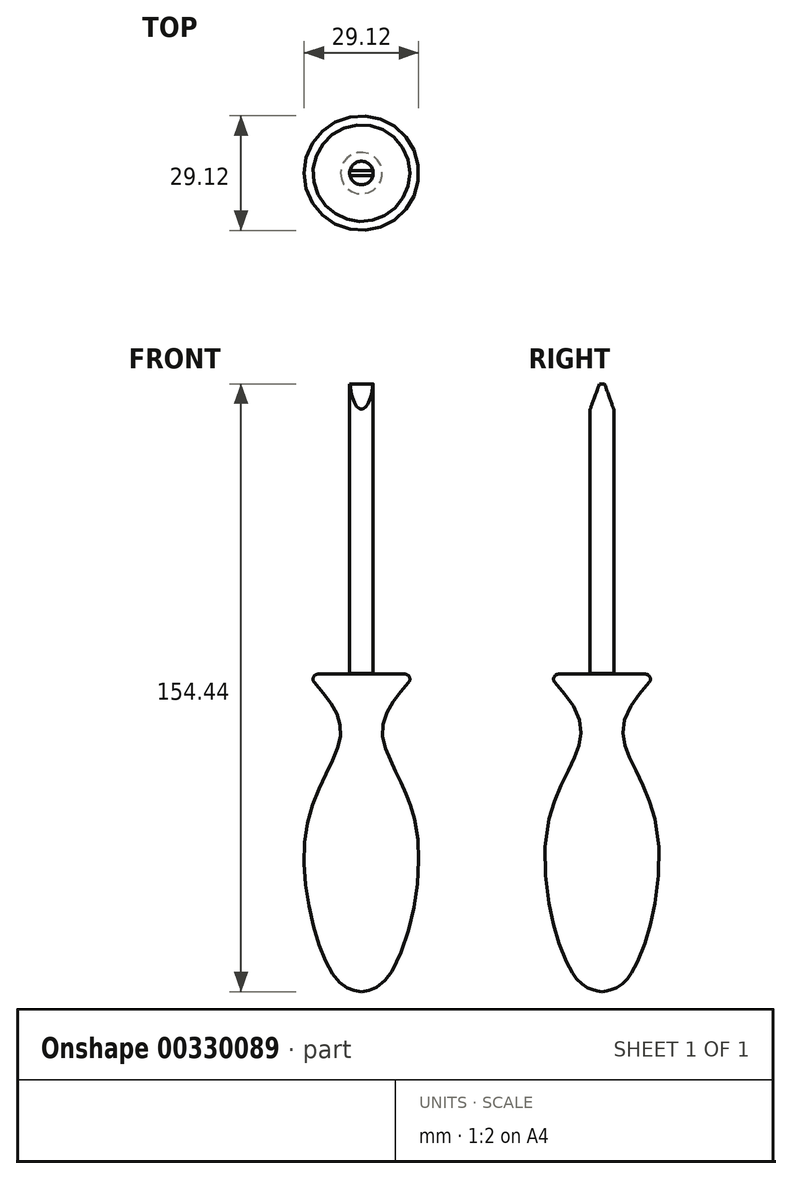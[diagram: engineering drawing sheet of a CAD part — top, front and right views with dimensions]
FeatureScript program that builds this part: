
annotation { "Feature Type Name" : "Feature", "Feature Type Description" : "" }
export const myFeature = defineFeature(function(context is Context, id is Id, definition is map)
    precondition{}
    {
        {
            var Q0;
            Q0=qCreatedBy(makeId("Front.planeOp"),FACE);
            var sketch = newSketch(context, id + "F0", { "sketchPlane" : qUnion([Q0])});
            skLineSegment(sketch, "E0", {"start": v(0, 12.38) * mm, "end": v(-13.91, 12.38) * mm});
            skFitSpline(sketch, "E1", {"points": [v(-13.91, 12.38) * mm, v(-5.27, -2.2) * mm, v(-13.91, -26.48) * mm, v(-6.62, -64.8) * mm, v(0, -68.31) * mm], "startDerivative": vector(57.37, -62.22) * mm, "endDerivative": vector(44.3, -7.4) * mm});
            skLineSegment(sketch, "E2", {"start": v(0, 12.38) * mm, "end": v(0, -68.31) * mm});
            skSolve(sketch);
        }
        {
            var Q0;
            Q0=makeQuery(id+"F0.imprint","IMPRINT",FACE,{"disambiguationData":[TD([[makeQuery(id+"F0.imprint","IMPRINT",EDGE,{"derivedFrom":sQuery(id+"F0.wireOp",EDGE,"E0")}),1.0]])]});
            var Q1;
            Q1=sQuery(id+"F0.wireOp",EDGE,"E2");
            revolve(context, id + "F1", {"entities" : qUnion([Q0]), "axis" : qUnion([Q1]), "revolveType" : RevolveType.FULL});
        }
        {
            var Q0;
            Q0=makeQuery(id+"F1.opRevolve","SWEPT_EDGE",EDGE,{"disambiguationData":[OSD([sQuery(id+"F0.wireOp",EDGE,"E0"),sQuery(id+"F0.wireOp",EDGE,"E1")])]});
            fillet(context, id + "F2", {"entities" : qUnion([Q0]), "radius" : 1.27 * mm, "tangentPropagation" : true, "allowEdgeOverflow" : false});
        }
        {
            var Q0;
            Q0=qCreatedBy(makeId("Front.planeOp"),FACE);
            var sketch = newSketch(context, id + "F3", { "sketchPlane" : qUnion([Q0])});
            skLineSegment(sketch, "E3", {"start": v(0, 12.56) * mm, "end": v(0, 86.13) * mm});
            skLineSegment(sketch, "E4", {"start": v(0, 86.13) * mm, "end": v(-3, 86.13) * mm});
            skLineSegment(sketch, "E5", {"start": v(-3, 86.13) * mm, "end": v(-3, 12.56) * mm});
            skLineSegment(sketch, "E6", {"start": v(-3, 12.56) * mm, "end": v(0, 12.56) * mm});
            skSolve(sketch);
        }
        {
            var Q0;
            Q0=makeQuery(id+"F3.imprint","IMPRINT",FACE,{"disambiguationData":[TD([[makeQuery(id+"F3.imprint","IMPRINT",EDGE,{"derivedFrom":sQuery(id+"F3.wireOp",EDGE,"E3")}),1.0]])]});
            var Q1;
            Q1=sQuery(id+"F3.wireOp",EDGE,"E3");
            revolve(context, id + "F4", {"entities" : qUnion([Q0]), "axis" : qUnion([Q1]), "revolveType" : RevolveType.FULL});
        }
        {
            var Q0;
            Q0=qCreatedBy(makeId("Top.planeOp"),FACE);
            cPlane(context, id + "F5", {"entities" : qUnion([Q0]), "cplaneType" : CPlaneType.OFFSET, "offset" : 96.52 * mm, "width" : 152.4 * mm, "height" : 152.4 * mm});
        }
        {
            var Q0;
            Q0=qCreatedBy(makeId("Top.planeOp"),FACE);
            cPlane(context, id + "F6", {"entities" : qUnion([Q0]), "cplaneType" : CPlaneType.OFFSET, "offset" : 86.06 * mm, "width" : 152.4 * mm, "height" : 152.4 * mm});
        }
        {
            var Q0;
            Q0=qCreatedBy(id+"F6.planeOp",FACE);
            var sketch = newSketch(context, id + "F7", { "sketchPlane" : qUnion([Q0])});
            skLineSegment(sketch, "E7", {"start": v(76.67, 0) * mm, "end": v(-76.37, 0) * mm, "construction": true});
            skSolve(sketch);
        }
        {
            var Q0;
            Q0=qCreatedBy(id+"F6.planeOp",FACE);
            var Q1;
            Q1=sQuery(id+"F7.wireOp",EDGE,"E7");
            cPlane(context, id + "F8", {"entities" : qUnion([Q0, Q1]), "cplaneType" : CPlaneType.LINE_ANGLE, "offset" : 25.4 * mm, "angle" : 20 * degree, "width" : 152.4 * mm, "height" : 152.4 * mm});
        }
        {
            var Q0;
            Q0=qCreatedBy(id+"F8.planeOp",FACE);
            var sketch = newSketch(context, id + "F9", { "sketchPlane" : qUnion([Q0])});
            skLineSegment(sketch, "E8.bottom", {"start": v(3.93, 30.07) * mm, "end": v(-3.82, 30.07) * mm});
            skLineSegment(sketch, "E8.top", {"start": v(3.93, 32.46) * mm, "end": v(-3.82, 32.46) * mm});
            skLineSegment(sketch, "E8.left", {"start": v(3.93, 30.07) * mm, "end": v(3.93, 32.46) * mm});
            skLineSegment(sketch, "E8.right", {"start": v(-3.82, 30.07) * mm, "end": v(-3.82, 32.46) * mm});
            skSolve(sketch);
        }
        {
            var Q0;
            Q0=makeQuery(id+"F9.imprint","IMPRINT",FACE,{"disambiguationData":[TD([[makeQuery(id+"F9.imprint","IMPRINT",EDGE,{"derivedFrom":sQuery(id+"F9.wireOp",EDGE,"E8.bottom")}),-1.0]])]});
            extrude(context, id + "F10", {"entities" : qUnion([Q0]), "operationType" : NewBodyOperationType.REMOVE, "depth" : 25.4 * mm});
        }
        {
            var Q0;
            Q0=qCreatedBy(id+"F6.planeOp",FACE);
            var Q1;
            Q1=sQuery(id+"F7.wireOp",EDGE,"E7");
            cPlane(context, id + "F11", {"entities" : qUnion([Q0, Q1]), "cplaneType" : CPlaneType.LINE_ANGLE, "offset" : 25.4 * mm, "angle" : 20 * degree, "oppositeDirection" : true, "width" : 152.4 * mm, "height" : 152.4 * mm});
        }
        {
            var Q0;
            Q0=qCreatedBy(id+"F11.planeOp",FACE);
            var sketch = newSketch(context, id + "F12", { "sketchPlane" : qUnion([Q0])});
            skLineSegment(sketch, "E9.bottom", {"start": v(-5.6, -30.07) * mm, "end": v(5.14, -30.07) * mm});
            skLineSegment(sketch, "E9.top", {"start": v(-5.6, -32.4) * mm, "end": v(5.14, -32.4) * mm});
            skLineSegment(sketch, "E9.left", {"start": v(-5.6, -30.07) * mm, "end": v(-5.6, -32.4) * mm});
            skLineSegment(sketch, "E9.right", {"start": v(5.14, -30.07) * mm, "end": v(5.14, -32.4) * mm});
            skSolve(sketch);
        }
        {
            var Q0;
            Q0=makeQuery(id+"F12.imprint","IMPRINT",FACE,{"disambiguationData":[TD([[makeQuery(id+"F12.imprint","IMPRINT",EDGE,{"derivedFrom":sQuery(id+"F12.wireOp",EDGE,"E9.bottom")}),-1.0]])]});
            extrude(context, id + "F13", {"entities" : qUnion([Q0]), "operationType" : NewBodyOperationType.REMOVE, "depth" : 25.4 * mm});
        }
    });
